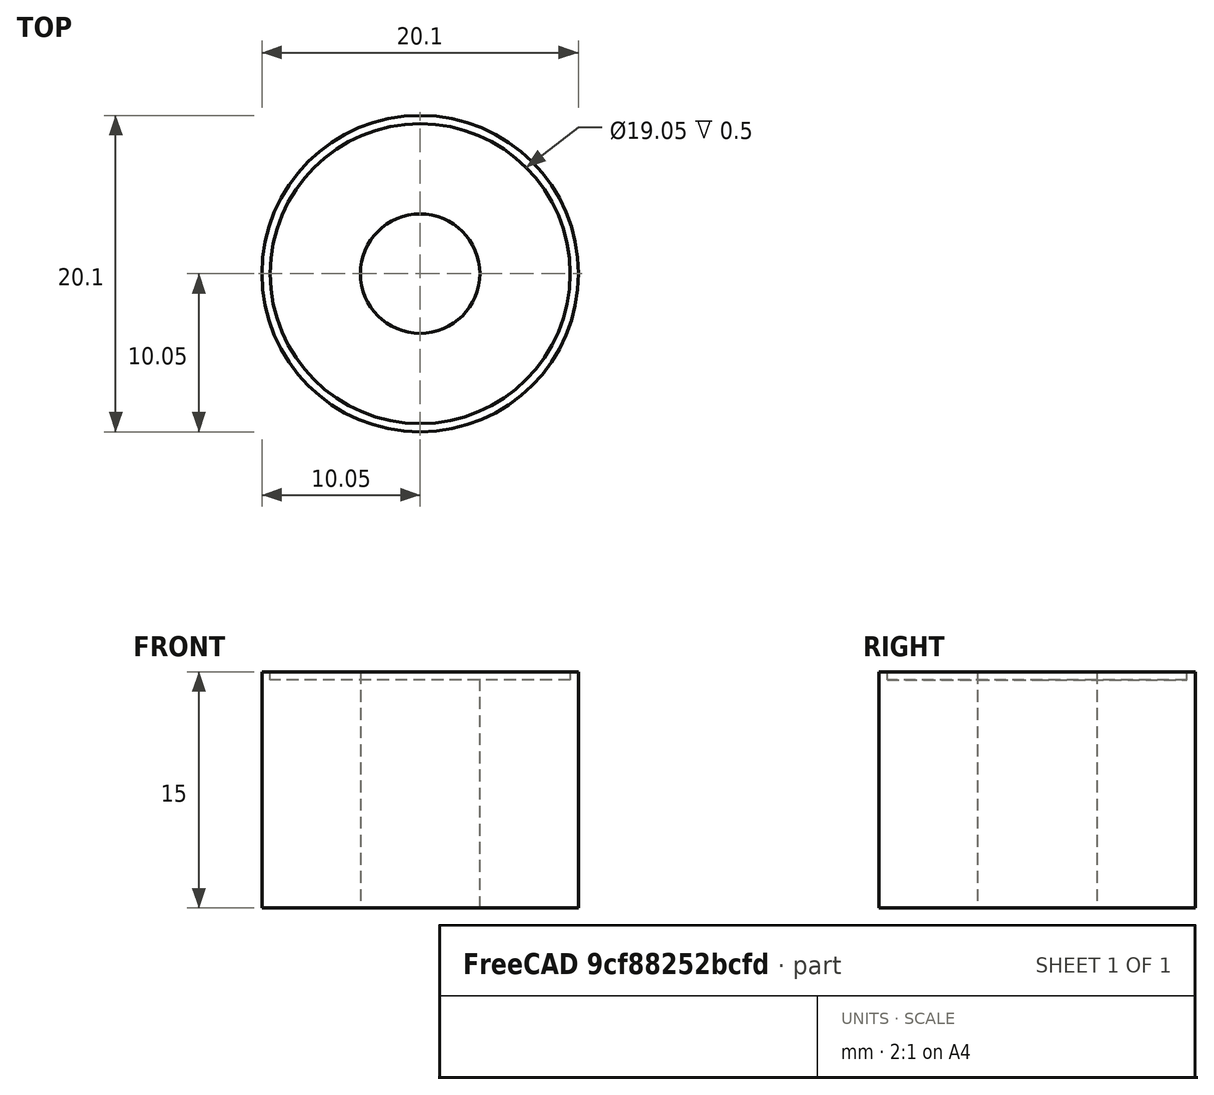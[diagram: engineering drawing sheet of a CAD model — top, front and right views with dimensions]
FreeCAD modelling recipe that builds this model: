
FCSTD DOCUMENT  (FreeCAD 0.20R29603 (Git))
Label: Eletro_Ima
License: All rights reserved
LicenseURL: http://en.wikipedia.org/wiki/All_rights_reserved
objects: Sketcher::SketchObject×3, PartDesign::Pad×2, PartDesign::Body×2, PartDesign::Pocket×1
note: 11 computed .brp shape members not serialized (recipe doc carries the construction recipe); baked Part::Feature solids carry a one-line shape summary decoded from their .brp

FEATURE [Sketcher::SketchObject] Sketch
  FullyConstrained = false
  MapMode = 5
  Support = -> [XY_Plane]
  sketch-geometry (1):
    g0: Circle CenterX=0 CenterY=0 CenterZ=0 NormalX=0 NormalY=0 NormalZ=1 AngleXU=0 Radius=10.0521
FEATURE [PartDesign::Pad] Pad
  Direction = (0,0,1)
  Length = 15
  Length2 = 10
  Profile = -> Sketch
  ReferenceAxis = -> Sketch [N_Axis]
  Type = 0
FEATURE [Sketcher::SketchObject] Sketch001
  FullyConstrained = false
  MapMode = 5
  Support = -> [XY_Plane001]
  sketch-geometry (1):
    g0: Circle CenterX=0 CenterY=0 CenterZ=0 NormalX=0 NormalY=0 NormalZ=1 AngleXU=0 Radius=3.79058
  constraints (1):
    c: Coincident(g0,g-1)
FEATURE [PartDesign::Pad] Pad001
  Direction = (0,0,1)
  Length = 15
  Length2 = 10
  Profile = -> Sketch001
  ReferenceAxis = -> Sketch001 [N_Axis]
  Type = 0
FEATURE [PartDesign::Body] Body001  label="Cilindro_Interno"
  Group = -> [Sketch001,Pad001]
  Origin = -> Origin001
  Tip = -> Pad001
FEATURE [Sketcher::SketchObject] Sketch002
  FullyConstrained = false
  MapMode = 5
  Placement = pos=(0,0,15) rot=(0,0,1;0rad)
  Support = -> [Pad]
  sketch-geometry (1):
    g0: Circle CenterX=0 CenterY=0 CenterZ=0 NormalX=0 NormalY=0 NormalZ=1 AngleXU=0 Radius=9.5235
  constraints (1):
    c: Coincident(g0,g-1)
FEATURE [PartDesign::Pocket] Pocket
  BaseFeature = -> Pad
  Direction = (0,0,-1)
  Length = 0.5
  Length2 = 5
  Profile = -> Sketch002
  ReferenceAxis = -> Sketch002 [N_Axis]
  Type = 0
FEATURE [PartDesign::Body] Body  label="Cilindro_Externo"
  Group = -> [Sketch,Pad,Sketch002,Pocket]
  Origin = -> Origin
  Tip = -> Pocket
